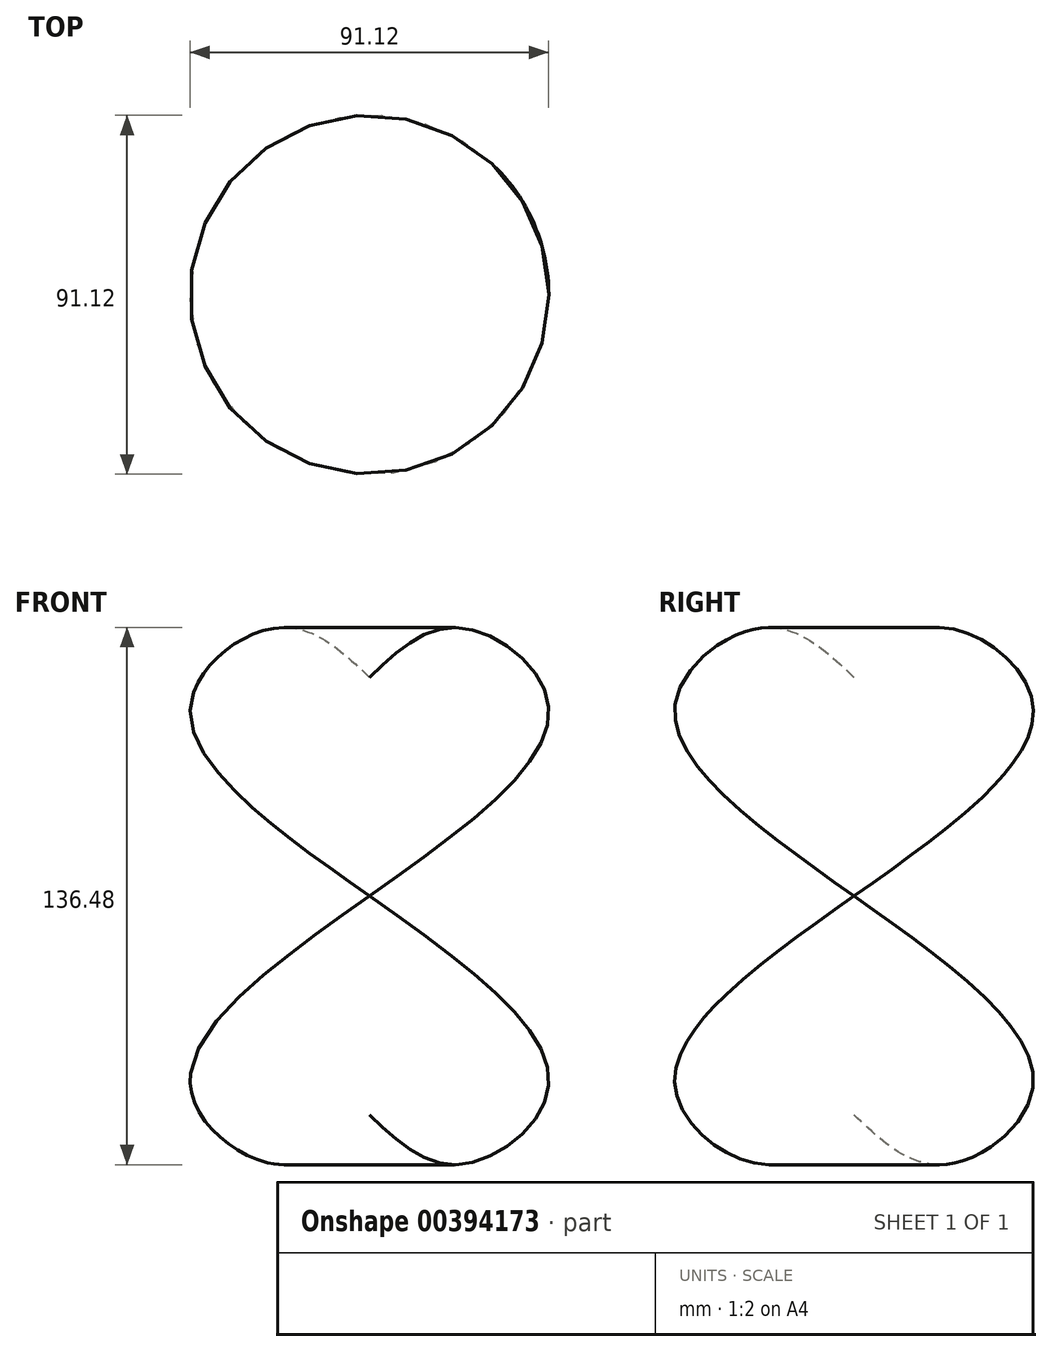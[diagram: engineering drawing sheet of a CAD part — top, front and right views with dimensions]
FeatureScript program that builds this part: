
annotation { "Feature Type Name" : "Feature", "Feature Type Description" : "" }
export const myFeature = defineFeature(function(context is Context, id is Id, definition is map)
    precondition{}
    {
        {
            var Q0;
            Q0=qCreatedBy(makeId("Front.planeOp"),FACE);
            var sketch = newSketch(context, id + "F0", { "sketchPlane" : qUnion([Q0])});
            skLineSegment(sketch, "E0", {"start": v(0, 75.87) * mm, "end": v(0, -76.07) * mm});
            skFitSpline(sketch, "E1", {"points": [v(0, 55.57) * mm, v(23.06, 68.19) * mm, v(45.52, 47.89) * mm, v(0, 0) * mm], "startDerivative": vector(77.02, 73.37) * mm, "endDerivative": vector(-161.56, -114.11) * mm});
            skLineSegment(sketch, "E2", {"start": v(-76.07, 0) * mm, "end": v(76.46, 0) * mm});
            skSolve(sketch);
        }
        {
            var Q0;
            {var subQ0=sQuery(id+"F0.wireOp",EDGE,"E1");Q0=makeQuery(id+"F0.imprint","IMPRINT",FACE,{"disambiguationData":[TD([[makeQuery(id+"F0.imprint","IMPRINT",EDGE,{"derivedFrom":subQ0}),-1.0]])]});}
            var Q1;
            Q1=sQuery(id+"F0.wireOp",EDGE,"240d805b-1562-4927-8e30-6afda32a8c0e");
            var Q2;
            Q2=sQuery(id+"F0.wireOp",EDGE,"e566f422-ee41-4e83-bf2a-ce4eda8c607a");
            var Q3;
            Q3=sQuery(id+"F0.wireOp",EDGE,"2395f097-b621-4318-a6c2-df22aa3660f9");
            var Q4;
            Q4=sQuery(id+"F0.wireOp",EDGE,"E0");
            revolve(context, id + "F1", {"entities" : qUnion([Q0]), "surfaceEntities" : qUnion([Q1, Q2, Q3]), "axis" : qUnion([Q4]), "revolveType" : RevolveType.FULL});
        }
        {
            var Q0;
            Q0=makeQuery(id+"F1.opRevolve","SWEPT_BODY",BODY,{"disambiguationData":[OSD([sQuery(id+"F0.wireOp",EDGE,"E0"),sQuery(id+"F0.wireOp",EDGE,"E1")])]});
            var Q1;
            Q1=qCreatedBy(makeId("Top.planeOp"),FACE);
            mirror(context, id + "F2", {"entities" : qUnion([Q0]), "mirrorPlane" : qUnion([Q1])});
        }
    });
